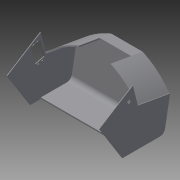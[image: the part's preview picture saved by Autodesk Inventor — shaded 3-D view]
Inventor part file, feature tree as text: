
AUTODESK INVENTOR PART (.ipt)
format: ipt  version: 2014 SP2 (Build 180246200, 246)  size: 239,616 bytes
history: native  units: in
note: dims shown in document units (in); Inventor stores cm internally (conversion verified against a paired STEP export)
features: extrude x12, sketch x12, fillet x1, mirror x1
ambient origin geometry x8: Origin, YZ Plane, XZ Plane, XY Plane, X Axis, Y Axis, Z Axis, Center Point
bodies: Solid1 (feature_tree)
feature tree (26):
  extrude  "Extrusion1"  Depth=3.0in
  extrude  "Extrusion2"  Depth=0.125in
  extrude  "Extrusion3"  Depth=8.75in
  sketch  "Sketch4"  dims[d8=1.5in d9=3.0in]
  extrude  "Extrusion5"  Depth=3.0in
  extrude  "Extrusion6"  Depth=0.125in
  extrude  "Extrusion8"  Depth=0.125in TaperAngle=0.0deg
  extrude  "Extrusion9"  Depth=0.125in
  extrude  "Extrusion10"  Depth=3.0in TaperAngle=0.0deg
  extrude  "Extrusion11"  Depth=4.0in
  fillet  "Fillet1"  Radius=2.8in
  mirror  "Mirror1"
  extrude  "Extrusion12"  Depth=0.0625in TaperAngle=0.0deg
  extrude  "Extrusion16"  Depth=0.5in
  extrude  "Extrusion17"  Depth=1.0in
  sketch  "Sketch1"  dims[d0=8.75in d1=3.0in]
  sketch  "Sketch2"  dims[d2=0.125in d3=0.0in d4=0.125in]
  sketch  "Sketch3"  dims[d5=8.75in d6=0.0in d7=2.9in]
  sketch  "Sketch5"  dims[d10=0.125in d11=0.0in d12=2.9in]
  sketch  "Sketch7"  dims[d15=12.0in d16=0.0in d17=0.125in d18=0.0in]
  sketch  "Sketch8"  dims[d24=0.125in d26=0.7874in d28=0.125in d29=0.3937in d31=1.0in]
  sketch  "Sketch9"  dims[d33=0.125in d34=3.0in d35=0.0in d36=0.0in d37=3.0in d38=0.0in]
  sketch  "Sketch10"  dims[d39=4.0in d40=4.8in d42=2.8in]
  sketch  "Sketch11"  dims[d44=3.7841in d45=0.0625in d46=0.0in]
  sketch  "Sketch15"  dims[d47=1.0in d48=0.0in d49=0.5in]
  sketch  "Sketch16"  dims[d50=2.85in d51=0.315in d52=12.0in d53=0.0in d82=1.0in d83=0.0in d84=0.145in d85=0.25in d86=0.145in d87=0.25in d88=0.145in d89=0.25in d90=1.0in d91=0.0in]
